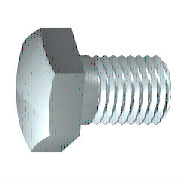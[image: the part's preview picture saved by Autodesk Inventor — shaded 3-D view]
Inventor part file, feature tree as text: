
AUTODESK INVENTOR PART (.ipt)
format: ipt  version: 2021 (Build 250183000, 183)  size: 189,440 bytes
history: native  units: mm (DEFAULTED — no unit token found)
features: sketch x3, extrude x1, chamfer x1, plane x1
ambient origin geometry x7: Origin, YZ Plane, XZ Plane, X Axis, Y Axis, Z Axis, Center Point
bodies: Solid1 (feature_tree), Body (feature_tree)
feature tree (6):
  extrude  "Head"  Depth=76.0mm
  chamfer  "Chamfer1"  Distance=4.7mm
  plane  "Work Plane1"
  sketch  "Sketch1"  dims[d0=80.0mm d1=76.0mm]
  sketch  "Sketch2"  dims[d2=8.0mm]
  sketch  "Sketch4"  dims[d12=90.0deg d3=4.7mm d4=0.0mm d5=30.0deg d21=90.0deg d6=0.766813mm d7=0.766912mm d8=0.0mm d9=0.6001mm d10=11.63mm d11=13.0mm d13=0.766912mm d14=8.0mm d15=76.0mm d16=0.0mm d19=13.0mm d55=45.0deg d57=0.0mm d58=0.0mm]
